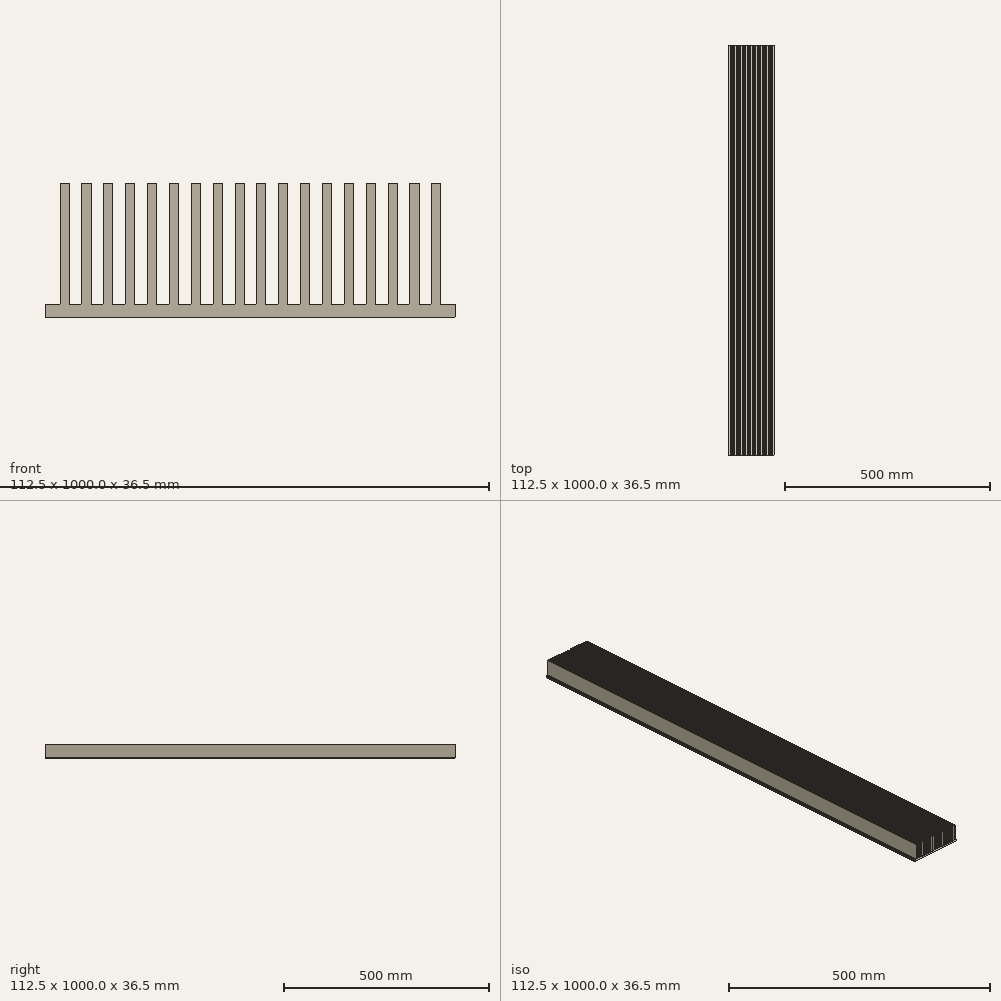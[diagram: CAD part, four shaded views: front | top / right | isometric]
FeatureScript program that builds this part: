
annotation { "Feature Type Name" : "Feature", "Feature Type Description" : "" }
export const myFeature = defineFeature(function(context is Context, id is Id, definition is map)
    precondition{}
    {
        {
            var Q0;
            Q0=qCreatedBy(makeId("Front.planeOp"),FACE);
            var sketch = newSketch(context, id + "F0", { "sketchPlane" : qUnion([Q0])});
            skLineSegment(sketch, "E0", {"start": v(0, 0) * mm, "end": v(56.25, 0) * mm});
            skLineSegment(sketch, "E1", {"start": v(56.25, 0) * mm, "end": v(56.25, 3.5) * mm});
            skLineSegment(sketch, "E2", {"start": v(56.25, 3.5) * mm, "end": v(52.25, 3.5) * mm});
            skLineSegment(sketch, "E3", {"start": v(52.25, 3.5) * mm, "end": v(52.25, 36.5) * mm});
            skLineSegment(sketch, "E4", {"start": v(52.25, 36.5) * mm, "end": v(49.75, 36.5) * mm});
            skLineSegment(sketch, "E5", {"start": v(49.75, 36.5) * mm, "end": v(49.75, 3.5) * mm});
            skLineSegment(sketch, "E6", {"start": v(0, 0) * mm, "end": v(-56.25, 0) * mm});
            skLineSegment(sketch, "E7", {"start": v(-56.25, 0) * mm, "end": v(-56.25, 3.5) * mm});
            skLineSegment(sketch, "E8", {"start": v(-56.25, 3.5) * mm, "end": v(-52.25, 3.5) * mm});
            skLineSegment(sketch, "E9", {"start": v(-52.25, 3.5) * mm, "end": v(-52.25, 55.1) * mm, "construction": true});
            skLineSegment(sketch, "E10", {"start": v(-52.25, 3.5) * mm, "end": v(49.75, 3.5) * mm});
            skLineSegment(sketch, "E11.1.0.0", {"start": v(46.25, 36.5) * mm, "end": v(43.75, 36.5) * mm});
            skLineSegment(sketch, "E11.1.0.1", {"start": v(46.25, 3.5) * mm, "end": v(46.25, 36.5) * mm});
            skLineSegment(sketch, "E11.1.0.2", {"start": v(43.75, 36.5) * mm, "end": v(43.75, 3.5) * mm});
            skLineSegment(sketch, "E11.2.0.0", {"start": v(40.25, 36.5) * mm, "end": v(37.75, 36.5) * mm});
            skLineSegment(sketch, "E11.2.0.1", {"start": v(40.25, 3.5) * mm, "end": v(40.25, 36.5) * mm});
            skLineSegment(sketch, "E11.2.0.2", {"start": v(37.75, 36.5) * mm, "end": v(37.75, 3.5) * mm});
            skLineSegment(sketch, "E11.3.0.0", {"start": v(34.25, 36.5) * mm, "end": v(31.75, 36.5) * mm});
            skLineSegment(sketch, "E11.3.0.1", {"start": v(34.25, 3.5) * mm, "end": v(34.25, 36.5) * mm});
            skLineSegment(sketch, "E11.3.0.2", {"start": v(31.75, 36.5) * mm, "end": v(31.75, 3.5) * mm});
            skLineSegment(sketch, "E11.4.0.0", {"start": v(28.25, 36.5) * mm, "end": v(25.75, 36.5) * mm});
            skLineSegment(sketch, "E11.4.0.1", {"start": v(28.25, 3.5) * mm, "end": v(28.25, 36.5) * mm});
            skLineSegment(sketch, "E11.4.0.2", {"start": v(25.75, 36.5) * mm, "end": v(25.75, 3.5) * mm});
            skLineSegment(sketch, "E11.5.0.0", {"start": v(22.25, 36.5) * mm, "end": v(19.75, 36.5) * mm});
            skLineSegment(sketch, "E11.5.0.1", {"start": v(22.25, 3.5) * mm, "end": v(22.25, 36.5) * mm});
            skLineSegment(sketch, "E11.5.0.2", {"start": v(19.75, 36.5) * mm, "end": v(19.75, 3.5) * mm});
            skLineSegment(sketch, "E11.6.0.0", {"start": v(16.25, 36.5) * mm, "end": v(13.75, 36.5) * mm});
            skLineSegment(sketch, "E11.6.0.1", {"start": v(16.25, 3.5) * mm, "end": v(16.25, 36.5) * mm});
            skLineSegment(sketch, "E11.6.0.2", {"start": v(13.75, 36.5) * mm, "end": v(13.75, 3.5) * mm});
            skLineSegment(sketch, "E11.7.0.0", {"start": v(10.25, 36.5) * mm, "end": v(7.75, 36.5) * mm});
            skLineSegment(sketch, "E11.7.0.1", {"start": v(10.25, 3.5) * mm, "end": v(10.25, 36.5) * mm});
            skLineSegment(sketch, "E11.7.0.2", {"start": v(7.75, 36.5) * mm, "end": v(7.75, 3.5) * mm});
            skLineSegment(sketch, "E11.8.0.0", {"start": v(4.25, 36.5) * mm, "end": v(1.75, 36.5) * mm});
            skLineSegment(sketch, "E11.8.0.1", {"start": v(4.25, 3.5) * mm, "end": v(4.25, 36.5) * mm});
            skLineSegment(sketch, "E11.8.0.2", {"start": v(1.75, 36.5) * mm, "end": v(1.75, 3.5) * mm});
            skLineSegment(sketch, "E11.9.0.0", {"start": v(-1.75, 36.5) * mm, "end": v(-4.25, 36.5) * mm});
            skLineSegment(sketch, "E11.9.0.1", {"start": v(-1.75, 3.5) * mm, "end": v(-1.75, 36.5) * mm});
            skLineSegment(sketch, "E11.9.0.2", {"start": v(-4.25, 36.5) * mm, "end": v(-4.25, 3.5) * mm});
            skLineSegment(sketch, "E11.10.0.0", {"start": v(-7.75, 36.5) * mm, "end": v(-10.25, 36.5) * mm});
            skLineSegment(sketch, "E11.10.0.1", {"start": v(-7.75, 3.5) * mm, "end": v(-7.75, 36.5) * mm});
            skLineSegment(sketch, "E11.10.0.2", {"start": v(-10.25, 36.5) * mm, "end": v(-10.25, 3.5) * mm});
            skLineSegment(sketch, "E11.11.0.0", {"start": v(-13.75, 36.5) * mm, "end": v(-16.25, 36.5) * mm});
            skLineSegment(sketch, "E11.11.0.1", {"start": v(-13.75, 3.5) * mm, "end": v(-13.75, 36.5) * mm});
            skLineSegment(sketch, "E11.11.0.2", {"start": v(-16.25, 36.5) * mm, "end": v(-16.25, 3.5) * mm});
            skLineSegment(sketch, "E11.12.0.0", {"start": v(-19.75, 36.5) * mm, "end": v(-22.25, 36.5) * mm});
            skLineSegment(sketch, "E11.12.0.1", {"start": v(-19.75, 3.5) * mm, "end": v(-19.75, 36.5) * mm});
            skLineSegment(sketch, "E11.12.0.2", {"start": v(-22.25, 36.5) * mm, "end": v(-22.25, 3.5) * mm});
            skLineSegment(sketch, "E11.13.0.0", {"start": v(-25.75, 36.5) * mm, "end": v(-28.25, 36.5) * mm});
            skLineSegment(sketch, "E11.13.0.1", {"start": v(-25.75, 3.5) * mm, "end": v(-25.75, 36.5) * mm});
            skLineSegment(sketch, "E11.13.0.2", {"start": v(-28.25, 36.5) * mm, "end": v(-28.25, 3.5) * mm});
            skLineSegment(sketch, "E11.14.0.0", {"start": v(-31.75, 36.5) * mm, "end": v(-34.25, 36.5) * mm});
            skLineSegment(sketch, "E11.14.0.1", {"start": v(-31.75, 3.5) * mm, "end": v(-31.75, 36.5) * mm});
            skLineSegment(sketch, "E11.14.0.2", {"start": v(-34.25, 36.5) * mm, "end": v(-34.25, 3.5) * mm});
            skLineSegment(sketch, "E11.15.0.0", {"start": v(-37.75, 36.5) * mm, "end": v(-40.25, 36.5) * mm});
            skLineSegment(sketch, "E11.15.0.1", {"start": v(-37.75, 3.5) * mm, "end": v(-37.75, 36.5) * mm});
            skLineSegment(sketch, "E11.15.0.2", {"start": v(-40.25, 36.5) * mm, "end": v(-40.25, 3.5) * mm});
            skLineSegment(sketch, "E11.16.0.0", {"start": v(-43.75, 36.5) * mm, "end": v(-46.25, 36.5) * mm});
            skLineSegment(sketch, "E11.16.0.1", {"start": v(-43.75, 3.5) * mm, "end": v(-43.75, 36.5) * mm});
            skLineSegment(sketch, "E11.16.0.2", {"start": v(-46.25, 36.5) * mm, "end": v(-46.25, 3.5) * mm});
            skLineSegment(sketch, "E11.17.0.0", {"start": v(-49.75, 36.5) * mm, "end": v(-52.25, 36.5) * mm});
            skLineSegment(sketch, "E11.17.0.1", {"start": v(-49.75, 3.5) * mm, "end": v(-49.75, 36.5) * mm});
            skLineSegment(sketch, "E11.17.0.2", {"start": v(-52.25, 36.5) * mm, "end": v(-52.25, 3.5) * mm});
            skLineSegment(sketch, "E11.direction1", {"start": v(49.75, 36.5) * mm, "end": v(43.75, 36.5) * mm, "construction": true});
            skSolve(sketch);
        }
        {
            var Q0;
            Q0 = qSketchRegion(id + "F0", true);
            extrude(context, id + "F1", {"entities" : qUnion([Q0]), "depth" : 1000 * mm});
        }
    });
